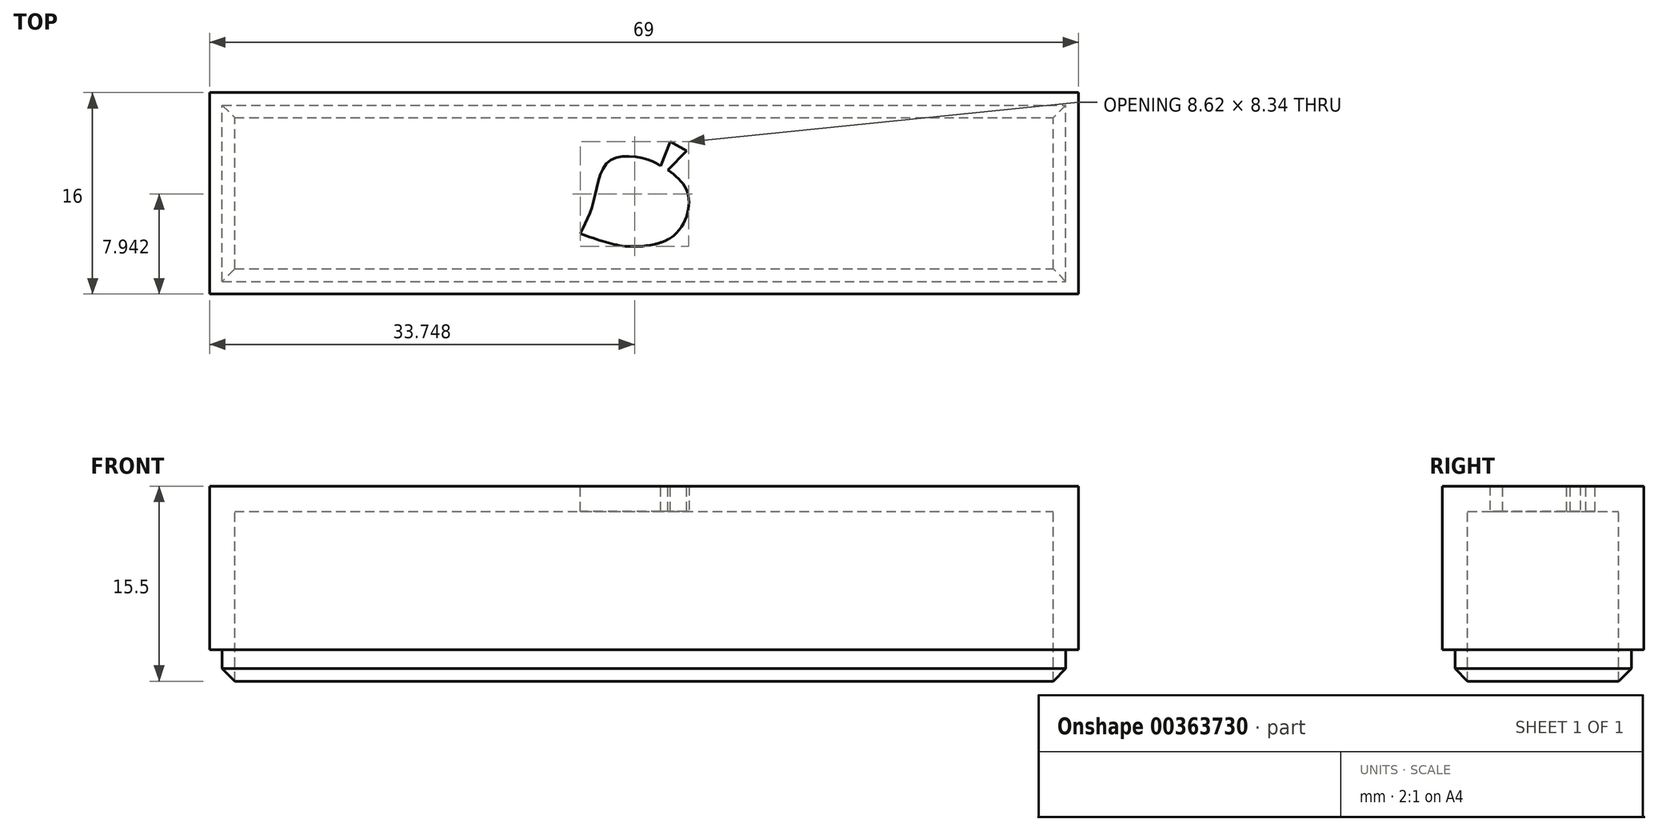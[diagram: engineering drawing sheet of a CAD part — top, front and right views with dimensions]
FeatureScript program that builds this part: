
annotation { "Feature Type Name" : "Feature", "Feature Type Description" : "" }
export const myFeature = defineFeature(function(context is Context, id is Id, definition is map)
    precondition{}
    {
        {
            var Q0;
            Q0=qCreatedBy(makeId("Top.planeOp"),FACE);
            var sketch = newSketch(context, id + "F0", { "sketchPlane" : qUnion([Q0])});
            skLineSegment(sketch, "E0.bottom", {"start": v(0, 0) * mm, "end": v(65, 0) * mm});
            skLineSegment(sketch, "E0.top", {"start": v(0, 12) * mm, "end": v(65, 12) * mm});
            skLineSegment(sketch, "E0.left", {"start": v(0, 0) * mm, "end": v(0, 12) * mm});
            skLineSegment(sketch, "E0.right", {"start": v(65, 0) * mm, "end": v(65, 12) * mm});
            skSolve(sketch);
        }
        {
            var Q0;
            Q0 = qSketchRegion(id + "F0", true);
            extrude(context, id + "F1", {"entities" : qUnion([Q0]), "oppositeDirection" : true, "depth" : 11 * mm});
        }
        {
            var Q0;
            Q0=makeQuery(id+"F1.opExtrude","CAP_FACE",FACE,{"disambiguationData":[OSD([sQuery(id+"F0.wireOp",EDGE,"E0.bottom"),sQuery(id+"F0.wireOp",EDGE,"E0.top"),sQuery(id+"F0.wireOp",EDGE,"E0.left"),sQuery(id+"F0.wireOp",EDGE,"E0.right")])],"isStart":false});
            shell(context, id + "F2", {"entities" : qUnion([Q0]), "thickness" : 2 * mm, "oppositeDirection" : true});
        }
        {
            var Q0;
            Q0=makeQuery(id+"F1.opExtrude","CAP_FACE",FACE,{"disambiguationData":[OSD([sQuery(id+"F0.wireOp",EDGE,"E0.bottom"),sQuery(id+"F0.wireOp",EDGE,"E0.top"),sQuery(id+"F0.wireOp",EDGE,"E0.left"),sQuery(id+"F0.wireOp",EDGE,"E0.right")])],"isStart":false});
            var sketch = newSketch(context, id + "F3", { "sketchPlane" : qUnion([Q0])});
            skLineSegment(sketch, "E1.bottom", {"start": v(-1, 1) * mm, "end": v(66, 1) * mm});
            skLineSegment(sketch, "E1.top", {"start": v(-1, -13) * mm, "end": v(66, -13) * mm});
            skLineSegment(sketch, "E1.left", {"start": v(-1, 1) * mm, "end": v(-1, -13) * mm});
            skLineSegment(sketch, "E1.right", {"start": v(66, 1) * mm, "end": v(66, -13) * mm});
            skLineSegment(sketch, "E2.bottom", {"start": v(0, 0) * mm, "end": v(65, 0) * mm});
            skLineSegment(sketch, "E2.top", {"start": v(0, -12) * mm, "end": v(65, -12) * mm});
            skLineSegment(sketch, "E2.left", {"start": v(0, 0) * mm, "end": v(0, -12) * mm});
            skLineSegment(sketch, "E2.right", {"start": v(65, 0) * mm, "end": v(65, -12) * mm});
            skSolve(sketch);
        }
        {
            var Q0;
            Q0 = qSketchRegion(id + "F3", true);
            extrude(context, id + "F4", {"entities" : qUnion([Q0]), "operationType" : NewBodyOperationType.ADD, "depth" : 2.5 * mm});
        }
        {
            var Q0;
            Q0=makeQuery(id+"F4.opExtrude","CAP_EDGE",EDGE,{"disambiguationData":[OSD([sQuery(id+"F3.wireOp",EDGE,"E1.bottom")])],"isStart":false});
            var Q1;
            Q1=makeQuery(id+"F4.opExtrude","CAP_EDGE",EDGE,{"disambiguationData":[OSD([sQuery(id+"F3.wireOp",EDGE,"E1.left")])],"isStart":false});
            var Q2;
            Q2=makeQuery(id+"F4.opExtrude","CAP_EDGE",EDGE,{"disambiguationData":[OSD([sQuery(id+"F3.wireOp",EDGE,"E1.top")])],"isStart":false});
            var Q3;
            Q3=makeQuery(id+"F4.opExtrude","CAP_EDGE",EDGE,{"disambiguationData":[OSD([sQuery(id+"F3.wireOp",EDGE,"E1.right")])],"isStart":false});
            chamfer(context, id + "F5", {"entities" : qUnion([Q0, Q1, Q2, Q3]), "width" : 1 * mm, "tangentPropagation" : true});
        }
        {
            var Q0;
            Q0=makeQuery(id+"F1.opExtrude","CAP_FACE",FACE,{"disambiguationData":[OSD([sQuery(id+"F0.wireOp",EDGE,"E0.bottom"),sQuery(id+"F0.wireOp",EDGE,"E0.top"),sQuery(id+"F0.wireOp",EDGE,"E0.left"),sQuery(id+"F0.wireOp",EDGE,"E0.right")])],"isStart":true});
            var sketch = newSketch(context, id + "F6", { "sketchPlane" : qUnion([Q0])});
            skPoint(sketch, "E3", {"position": v(32, 11.72) * mm});
            skPoint(sketch, "E4", {"position": v(31.95, -0.2) * mm});
            skLineSegment(sketch, "E5", {"start": v(33.82, 8.16) * mm, "end": v(34.58, 10.11) * mm});
            skLineSegment(sketch, "E6", {"start": v(34.58, 10.11) * mm, "end": v(35.88, 9.39) * mm});
            skLineSegment(sketch, "E7", {"start": v(35.88, 9.39) * mm, "end": v(34.4, 7.86) * mm});
            skPoint(sketch, "E8.1.internal.snap0", {"position": v(35.14, 8.63) * mm});
            skPoint(sketch, "E8.2.internal.snap0", {"position": v(35.14, 8.63) * mm});
            skFitSpline(sketch, "E8", {"points": [v(33.82, 8.16) * mm, v(32.95, 8.63) * mm, v(29.83, 8.63) * mm, v(28.52, 5.47) * mm, v(27.44, 2.79) * mm], "startDerivative": vector(-4.08, 3.01) * mm, "endDerivative": vector(-4.53, -9.04) * mm});
            skFitSpline(sketch, "E9", {"points": [v(27.44, 2.79) * mm, v(29.68, 2.06) * mm, v(31.5, 1.77) * mm, v(34.56, 2.43) * mm, v(35.98, 4.55) * mm, v(35.77, 6.49) * mm, v(34.4, 7.86) * mm], "startDerivative": vector(13.9, -4.73) * mm, "endDerivative": vector(-10.42, 8.05) * mm});
            skPoint(sketch, "E10", {"position": v(33.3, 1.94) * mm});
            skFitSpline(sketch, "E11", {"points": [v(33.3, 1.94) * mm, v(32.4, 2.56) * mm, v(32.28, 3.86) * mm, v(33.3, 4.68) * mm, v(34.3, 4.5) * mm, v(34.86, 3.69) * mm, v(34.56, 2.43) * mm], "startDerivative": vector(-6.38, 2.84) * mm, "endDerivative": vector(-3.05, -7.42) * mm});
            skSolve(sketch);
        }
        {
            var Q0;
            Q0 = qSketchRegion(id + "F6", true);
            extrude(context, id + "F7", {"entities" : qUnion([Q0]), "operationType" : NewBodyOperationType.REMOVE, "endBound" : BoundingType.UP_TO_NEXT, "oppositeDirection" : true, "depth" : 25 * mm});
        }
    });
